# Revit family: Emergency_Equipment-Haws_Corporation-Shower_8720
name_source: partatom
category: Plumbing Fixtures
revit_build: Autodesk Revit 2018 (Build: 20170223_1515(x64)
units: mm (PartAtom-declared; Revit-internal decimal feet)

## family parameters
Always vertical = Yes
Cut with Voids When Loaded = No
OmniClass Number = 23.45.05.14.17
OmniClass Title = Showers
Part Type = Normal
Room Calculation Point = No
Round Connector Dimension = Use Diameter
Shared = No
Work Plane-Based = No

## types (1)
- 8720 - Outdoor Overhead Tank Combination Shower
    Apparent Load = 480 VA
    Assembly Code = D2010710
    Depth = 57 1/2"
    Description = Outdoor Overhead Tank Combination Shower
    Edition number = 1
    Finish = Metal - Haws Corporation - Green
    Flow = 20 GPM
    HW Connection = No
    Height = 179"
    Keynote = S12
    Manufacturer = Haws Corporation
    Model = 8720
    Number of Poles = 1
    Phase = 3
    Power Factor = 1
    Product Guid = 25d8a02b-88f5-4a3c-8b54-5a61e6ed3ac6
    Product data url = https://bimobject.com
    Sanitary Diameter = 2 3/4"
    Supply Diameter = 1 1/2"
    URL = https://www.hawsco.com
    Vent Connection = No
    Voltage = 480 V
    Width = 60 3/4"

## geometry (parser evidence)
native form markers: Sweep x4
no freeform markers — native parametric forms only
